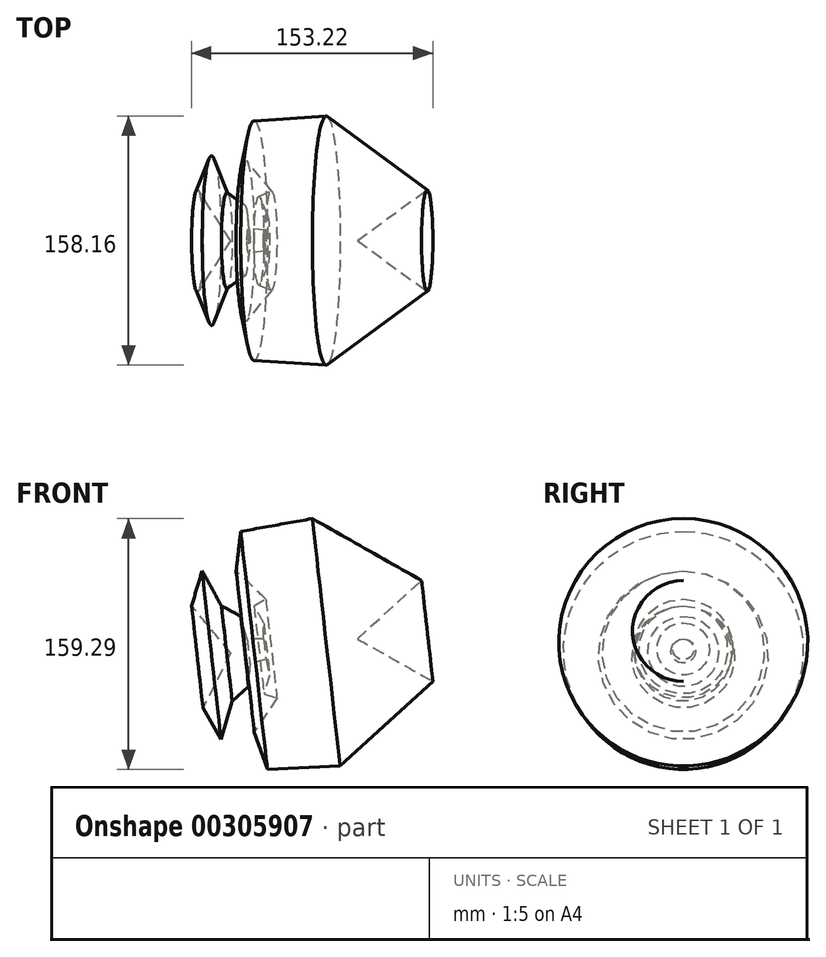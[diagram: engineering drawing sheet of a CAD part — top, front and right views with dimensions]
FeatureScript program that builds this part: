
annotation { "Feature Type Name" : "Feature", "Feature Type Description" : "" }
export const myFeature = defineFeature(function(context is Context, id is Id, definition is map)
    precondition{}
    {
        {
            var Q0;
            Q0=qCreatedBy(makeId("Front.planeOp"),FACE);
            var sketch = newSketch(context, id + "F0", { "sketchPlane" : qUnion([Q0])});
            skLineSegment(sketch, "E0", {"start": v(-42.26, -34.25) * mm, "end": v(38.18, -25.21) * mm});
            skLineSegment(sketch, "E1", {"start": v(38.18, -25.21) * mm, "end": v(-13.12, 31.63) * mm});
            skLineSegment(sketch, "E2", {"start": v(-13.12, 31.63) * mm, "end": v(-35.85, 43) * mm});
            skLineSegment(sketch, "E3", {"start": v(-35.85, 43) * mm, "end": v(9.62, 51.15) * mm});
            skLineSegment(sketch, "E4", {"start": v(9.62, 51.15) * mm, "end": v(78.99, 11.8) * mm});
            skLineSegment(sketch, "E5", {"start": v(78.99, 11.8) * mm, "end": v(38.18, -25.21) * mm});
            skLineSegment(sketch, "E6", {"start": v(-42.26, -34.25) * mm, "end": v(-67.04, -4.23) * mm});
            skLineSegment(sketch, "E7", {"start": v(-67.04, -4.23) * mm, "end": v(-60.34, 17.93) * mm});
            skLineSegment(sketch, "E8", {"start": v(-60.34, 17.93) * mm, "end": v(-48.1, -4.23) * mm});
            skLineSegment(sketch, "E9", {"start": v(-48.1, -4.23) * mm, "end": v(-35.85, -10.93) * mm});
            skLineSegment(sketch, "E10", {"start": v(-35.85, -10.93) * mm, "end": v(-31.77, -25.21) * mm});
            skLineSegment(sketch, "E11", {"start": v(-31.77, -25.21) * mm, "end": v(-21.28, -25.21) * mm});
            skLineSegment(sketch, "E12", {"start": v(-21.28, -25.21) * mm, "end": v(-21.28, -14.43) * mm});
            skLineSegment(sketch, "E13", {"start": v(-21.28, -15.01) * mm, "end": v(-27.4, -4.23) * mm});
            skLineSegment(sketch, "E14", {"start": v(-27.4, -4.23) * mm, "end": v(-19.95, 0) * mm});
            skLineSegment(sketch, "E15", {"start": v(-19.95, 0) * mm, "end": v(-38.77, 17.93) * mm});
            skLineSegment(sketch, "E16", {"start": v(-38.77, 17.93) * mm, "end": v(-60.34, 17.93) * mm});
            skLineSegment(sketch, "E17", {"start": v(-38.77, 17.93) * mm, "end": v(-35.85, 43) * mm});
            skSolve(sketch);
        }
        {
            var Q0;
            Q0=makeQuery(id+"F0.imprint","IMPRINT",FACE,{"disambiguationData":[TD([[makeQuery(id+"F0.imprint","IMPRINT",EDGE,{"derivedFrom":sQuery(id+"F0.wireOp",EDGE,"E0")}),1.0]])]});
            var Q1;
            Q1=makeQuery(id+"F0.imprint","IMPRINT",FACE,{"disambiguationData":[TD([[makeQuery(id+"F0.imprint","IMPRINT",EDGE,{"derivedFrom":sQuery(id+"F0.wireOp",EDGE,"E1")}),-1.0]])]});
            var Q2;
            Q2=sQuery(id+"F0.wireOp",EDGE,"E0");
            revolve(context, id + "F1", {"entities" : qUnion([Q0, Q1]), "axis" : qUnion([Q2]), "revolveType" : RevolveType.FULL});
        }
    });
